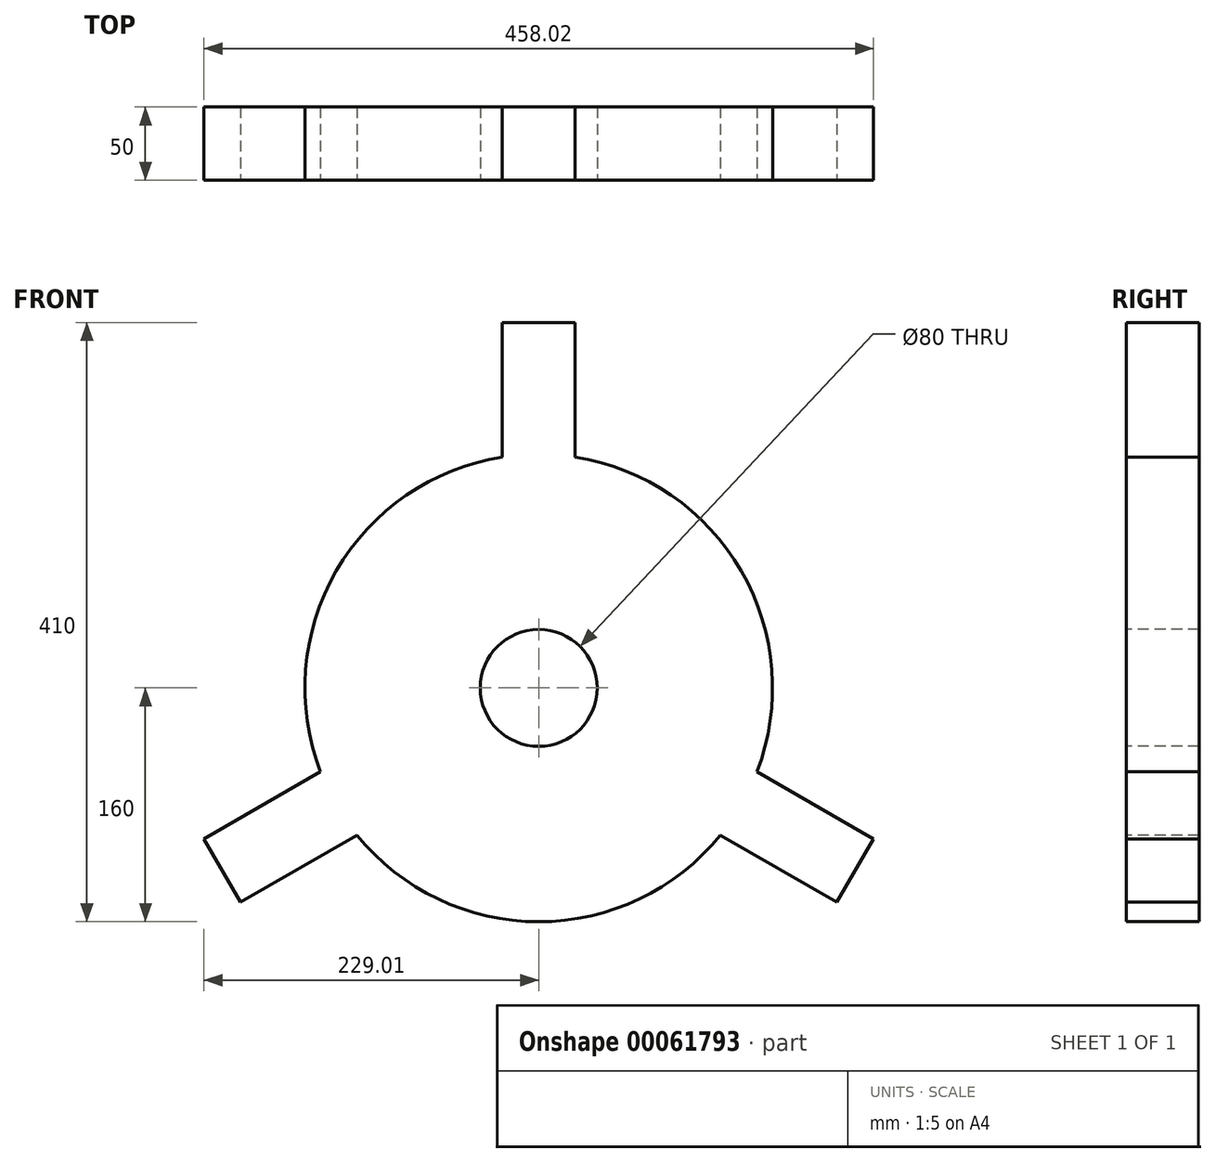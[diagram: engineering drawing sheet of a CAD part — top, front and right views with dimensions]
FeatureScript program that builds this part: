
annotation { "Feature Type Name" : "Feature", "Feature Type Description" : "" }
export const myFeature = defineFeature(function(context is Context, id is Id, definition is map)
    precondition{}
    {
        {
            var Q0;
            Q0=qCreatedBy(makeId("Front.planeOp"),FACE);
            var sketch = newSketch(context, id + "F0", { "sketchPlane" : qUnion([Q0])});
            skArc(sketch, "E0", {"start": v(-25, 158.03) * mm, "mid": v(-138.56, 80) * mm, "end": v(-149.36, -57.37) * mm});
            skLineSegment(sketch, "E1.rect.bottom", {"start": v(25, 250) * mm, "end": v(-25, 250) * mm});
            skLineSegment(sketch, "E1.rect.left", {"start": v(25, 250) * mm, "end": v(25, 158.03) * mm});
            skLineSegment(sketch, "E1.rect.right", {"start": v(-25, 250) * mm, "end": v(-25, 158.03) * mm});
            skPoint(sketch, "E1.rect.top.start.orphan", {"position": v(25, -250) * mm});
            skPoint(sketch, "E2.orphan", {"position": v(-25, -250) * mm});
            skLineSegment(sketch, "E3.1.0", {"start": v(-204, -146.65) * mm, "end": v(-124.36, -100.67) * mm});
            skLineSegment(sketch, "E3.1.1", {"start": v(-229, -103.35) * mm, "end": v(-204, -146.65) * mm});
            skLineSegment(sketch, "E3.1.2", {"start": v(-229, -103.35) * mm, "end": v(-149.36, -57.37) * mm});
            skLineSegment(sketch, "E3.2.0", {"start": v(229, -103.35) * mm, "end": v(149.36, -57.37) * mm});
            skLineSegment(sketch, "E3.2.1", {"start": v(204, -146.65) * mm, "end": v(229, -103.35) * mm});
            skLineSegment(sketch, "E3.2.2", {"start": v(204, -146.65) * mm, "end": v(124.36, -100.67) * mm});
            skArc(sketch, "E4.trimOffspring", {"start": v(-124.36, -100.67) * mm, "mid": v(0, -160) * mm, "end": v(124.36, -100.67) * mm});
            skArc(sketch, "E5.trimOffspring", {"start": v(149.36, -57.37) * mm, "mid": v(138.56, 80) * mm, "end": v(25, 158.03) * mm});
            skCircle(sketch, "E6", {"center": v(0, 0) * mm, "radius": 40 * mm});
            skSolve(sketch);
        }
        {
            var Q0;
            Q0=makeQuery(id+"F0.imprint","IMPRINT",FACE,{"disambiguationData":[TD([[makeQuery(id+"F0.imprint","IMPRINT",EDGE,{"derivedFrom":sQuery(id+"F0.wireOp",EDGE,"E0")}),1.0]])]});
            extrude(context, id + "F1", {"entities" : qUnion([Q0]), "oppositeDirection" : true, "depth" : 50 * mm});
        }
    });
